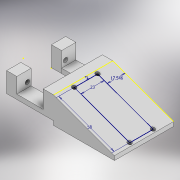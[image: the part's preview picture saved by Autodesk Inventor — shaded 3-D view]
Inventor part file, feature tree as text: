
AUTODESK INVENTOR PART (.ipt)
format: ipt  version: 2021 (Build 250183000, 183)  size: 199,680 bytes
history: native  units: mm
features: thicken_offset x6, sketch x6, extrude x4, chamfer x1, hole x1
ambient origin geometry x8: Origin, YZ Plane, XZ Plane, XY Plane, X Axis, Y Axis, Z Axis, Center Point
bodies: Solid1 (feature_tree)
feature tree (18):
  extrude  "Extrusion1"  Depth=10.0mm
  extrude  "Extrusion2"  Depth=10.0mm
  thicken_offset  "Thicken1"
  sketch  "Sketch3"  dims[d5=10.0mm d6=5.0mm]
  thicken_offset  "Thicken2"
  thicken_offset  "Thicken3"
  thicken_offset  "Thicken4"
  thicken_offset  "Thicken5"
  extrude  "Extrusion3"  Depth=10.0mm
  thicken_offset  "Thicken6"
  extrude  "Extrusion4"  Depth=4.0mm
  chamfer  "Chamfer2"  Distance=4.0mm
  hole  "Hole1"  [1 undecoded]
  sketch  "Sketch1"  dims[d0=10.0mm d1=10.0mm]
  sketch  "Sketch2"  dims[d2=10.0mm d3=0.0mm d4=5.0mm]
  sketch  "Sketch4"  dims[d7=26.0mm d8=0.0mm d9=4.0mm]
  sketch  "Sketch5"  dims[d10=4.0mm]
  sketch  "Sketch7"  dims[d11=4.0mm d12=4.0mm d13=4.0mm d14=4.0mm d15=0.4mm d16=0.4mm d17=0.4mm d18=0.4mm d19=10.0mm d20=70.0mm d21=0.0mm d22=12.0mm d23=32.0mm d24=60.0mm d25=4.0mm d26=0.0mm d30=60.0mm d31=2.0mm d32=3.490659mm d33=23.0mm d34=58.0mm d35=3.0mm d36=17.546mm d37=4.0mm d38=6.0mm d39=4.0mm d40=2.0mm d41=90.0deg d42=8.0mm d43=20.594885mm]
note: 1 required parameter value undecoded (feature->parameter linkage not recoverable at this tier; creation-order binding heuristic only, values carry confidence <= 0.55)
